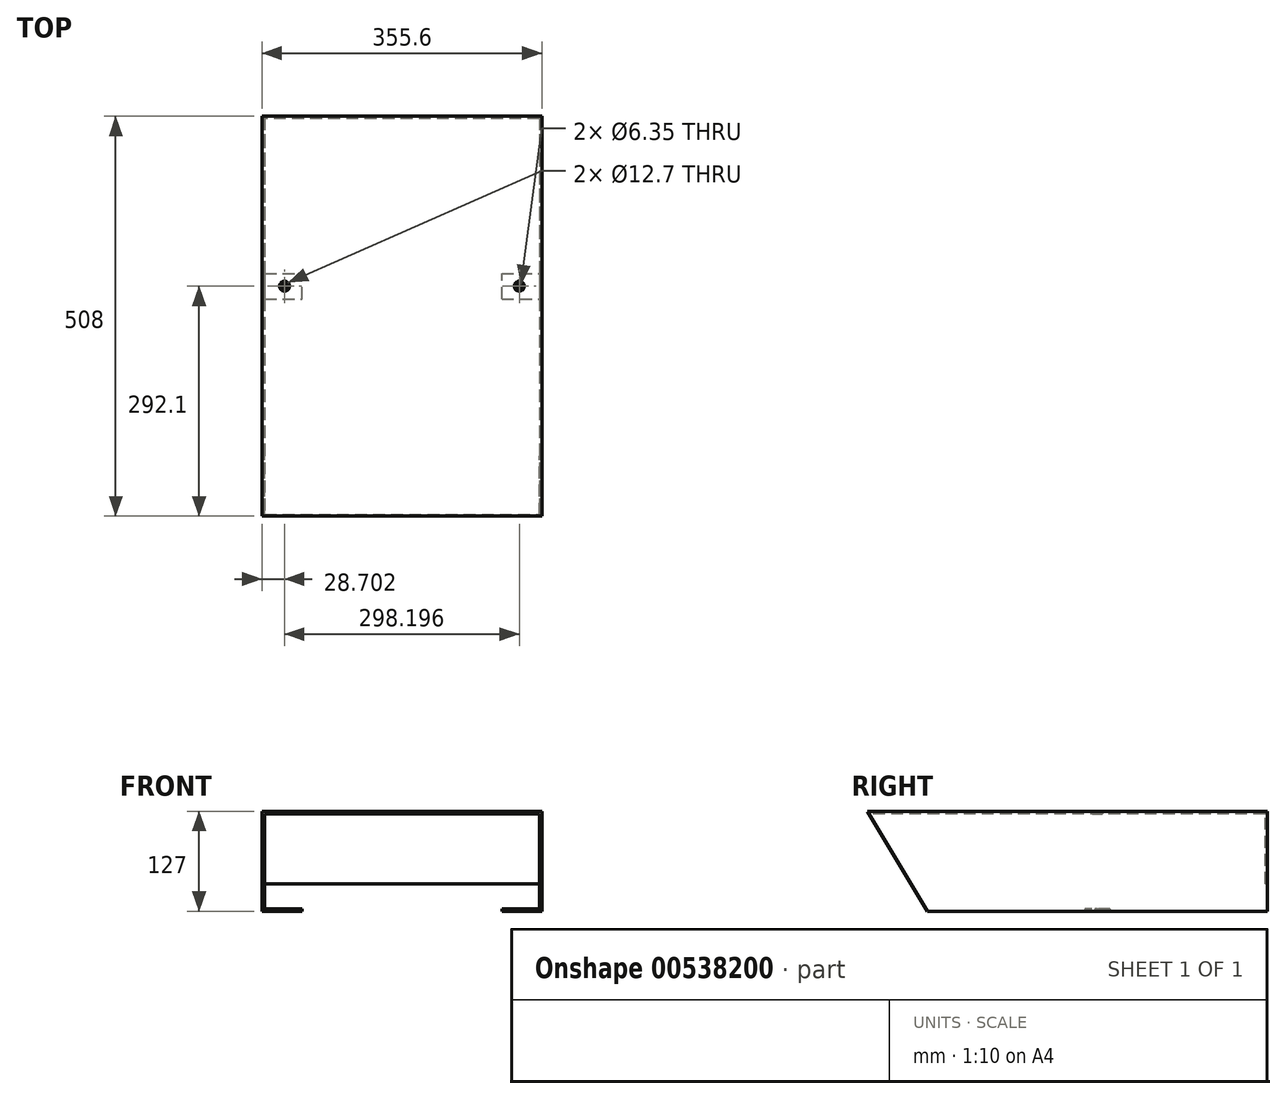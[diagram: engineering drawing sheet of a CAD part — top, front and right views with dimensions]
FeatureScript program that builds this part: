
annotation { "Feature Type Name" : "Feature", "Feature Type Description" : "" }
export const myFeature = defineFeature(function(context is Context, id is Id, definition is map)
    precondition{}
    {
        {
            var Q0;
            Q0=qCreatedBy(makeId("Front.planeOp"),FACE);
            var sketch = newSketch(context, id + "F0", { "sketchPlane" : qUnion([Q0])});
            skLineSegment(sketch, "E0.bottom", {"start": v(-177.8, 63.5) * mm, "end": v(177.8, 63.5) * mm});
            skLineSegment(sketch, "E0.top", {"start": v(-177.8, -63.5) * mm, "end": v(177.8, -63.5) * mm});
            skLineSegment(sketch, "E0.left", {"start": v(-177.8, 63.5) * mm, "end": v(-177.8, -63.5) * mm});
            skLineSegment(sketch, "E0.right", {"start": v(177.8, 63.5) * mm, "end": v(177.8, -63.5) * mm});
            skPoint(sketch, "E0.middle", {"position": v(0, 0) * mm});
            skSolve(sketch);
        }
        {
            var Q0;
            Q0=qCreatedBy(makeId("Front.planeOp"),FACE);
            var sketch = newSketch(context, id + "F1", { "sketchPlane" : qUnion([Q0])});
            skLineSegment(sketch, "E1.0", {"start": v(-177.8, 63.5) * mm, "end": v(-177.8, -63.5) * mm});
            skLineSegment(sketch, "E2.0", {"start": v(-177.8, 63.5) * mm, "end": v(177.8, 63.5) * mm});
            skLineSegment(sketch, "E3.0", {"start": v(177.8, 63.5) * mm, "end": v(177.8, -63.5) * mm});
            skLineSegment(sketch, "E4.0", {"start": v(-174.5, 60.2) * mm, "end": v(-174.5, -63.5) * mm});
            skLineSegment(sketch, "E4.1", {"start": v(-174.5, 60.2) * mm, "end": v(174.5, 60.2) * mm});
            skLineSegment(sketch, "E4.2", {"start": v(174.5, 60.2) * mm, "end": v(174.5, -63.5) * mm});
            skLineSegment(sketch, "E5", {"start": v(-177.8, -63.5) * mm, "end": v(-174.5, -63.5) * mm});
            skLineSegment(sketch, "E6", {"start": v(174.5, -63.5) * mm, "end": v(177.8, -63.5) * mm});
            skSolve(sketch);
        }
        {
            var Q0;
            Q0 = qSketchRegion(id + "F1", true);
            extrude(context, id + "F2", {"entities" : qUnion([Q0]), "endBound" : BoundingType.SYMMETRIC, "oppositeDirection" : true, "depth" : 431.8 * mm, "offsetDistance" : 25.4 * mm});
        }
        {
            var Q0;
            Q0=makeQuery(id+"F2.opExtrude","CAP_FACE",FACE,{"disambiguationData":[OSD([sQuery(id+"F1.wireOp",EDGE,"E1.0"),sQuery(id+"F1.wireOp",EDGE,"E2.0"),sQuery(id+"F1.wireOp",EDGE,"E3.0"),sQuery(id+"F1.wireOp",EDGE,"E4.0"),sQuery(id+"F1.wireOp",EDGE,"E4.1"),sQuery(id+"F1.wireOp",EDGE,"E4.2"),sQuery(id+"F1.wireOp",EDGE,"E5"),sQuery(id+"F1.wireOp",EDGE,"E6")])],"isStart":true});
            extrude(context, id + "F3", {"entities" : qUnion([Q0]), "operationType" : NewBodyOperationType.ADD, "depth" : 76.2 * mm, "offsetDistance" : 25.4 * mm});
        }
        {
            var Q0;
            {var subQ0=sQuery(id+"F1.wireOp",EDGE,"E3.0");Q0=makeQuery(id+"F3.boolean.opBoolean","MERGE",FACE,{"derivedFrom":[makeQuery(id+"F2.opExtrude","SWEPT_FACE",FACE,{"disambiguationData":[OSD([subQ0])]}),makeQuery(id+"F3.opExtrude","SWEPT_FACE",FACE,{"disambiguationData":[OSD([subQ0])]})]});}
            var sketch = newSketch(context, id + "F4", { "sketchPlane" : qUnion([Q0])});
            skLineSegment(sketch, "E7.bottom", {"start": v(215.9, 63.5) * mm, "end": v(-215.9, 63.5) * mm});
            skLineSegment(sketch, "E7.top", {"start": v(215.9, -63.5) * mm, "end": v(-215.9, -63.5) * mm});
            skLineSegment(sketch, "E7.left", {"start": v(215.9, 63.5) * mm, "end": v(215.9, -63.5) * mm});
            skLineSegment(sketch, "E7.right", {"start": v(-215.9, 63.5) * mm, "end": v(-215.9, -63.5) * mm});
            skPoint(sketch, "E7.middle", {"position": v(0, 0) * mm});
            skLineSegment(sketch, "E8", {"start": v(-215.9, -63.5) * mm, "end": v(-292.1, 63.5) * mm});
            skLineSegment(sketch, "E9", {"start": v(-292.1, 63.5) * mm, "end": v(-292.1, -63.5) * mm});
            skLineSegment(sketch, "E10", {"start": v(-292.1, -63.5) * mm, "end": v(-215.9, -63.5) * mm});
            skSolve(sketch);
        }
        {
            var Q0;
            Q0=makeQuery(id+"F4.imprint","IMPRINT",FACE,{"disambiguationData":[TD([[makeQuery(id+"F4.imprint","IMPRINT",EDGE,{"derivedFrom":sQuery(id+"F4.wireOp",EDGE,"E8")}),1.0]])]});
            extrude(context, id + "F5", {"entities" : qUnion([Q0]), "operationType" : NewBodyOperationType.REMOVE, "oppositeDirection" : true, "depth" : 375.92 * mm, "offsetDistance" : 25.4 * mm, "hasSecondDirection" : true, "secondDirectionOppositeDirection" : false, "secondDirectionDepth" : 25.4 * mm});
        }
        {
            var Q0;
            {var subQ0=sQuery(id+"F1.wireOp",EDGE,"E4.0");Q0=makeQuery(id+"F3.boolean.opBoolean","MERGE",FACE,{"derivedFrom":[makeQuery(id+"F2.opExtrude","SWEPT_FACE",FACE,{"disambiguationData":[OSD([subQ0])]}),makeQuery(id+"F3.opExtrude","SWEPT_FACE",FACE,{"disambiguationData":[OSD([subQ0])]})]});}
            var sketch = newSketch(context, id + "F6", { "sketchPlane" : qUnion([Q0])});
            skLineSegment(sketch, "E11", {"start": v(215.9, 60.2) * mm, "end": v(213.1, 60.2) * mm});
            skLineSegment(sketch, "E12", {"start": v(213.1, 60.2) * mm, "end": v(213.1, -28.7) * mm});
            skLineSegment(sketch, "E13", {"start": v(213.1, -28.7) * mm, "end": v(215.9, -28.7) * mm});
            skLineSegment(sketch, "E14", {"start": v(215.9, -28.7) * mm, "end": v(215.9, 60.2) * mm});
            skSolve(sketch);
        }
        {
            var Q0;
            Q0=makeQuery(id+"F6.imprint","IMPRINT",FACE,{"disambiguationData":[TD([[makeQuery(id+"F6.imprint","IMPRINT",EDGE,{"derivedFrom":sQuery(id+"F6.wireOp",EDGE,"E11")}),1.0]])]});
            var Q1;
            {var subQ0=sQuery(id+"F1.wireOp",EDGE,"E4.2");Q1=makeQuery(id+"F3.boolean.opBoolean","MERGE",FACE,{"derivedFrom":[makeQuery(id+"F2.opExtrude","SWEPT_FACE",FACE,{"disambiguationData":[OSD([subQ0])]}),makeQuery(id+"F3.opExtrude","SWEPT_FACE",FACE,{"disambiguationData":[OSD([subQ0])]})]});}
            extrude(context, id + "F7", {"entities" : qUnion([Q0]), "operationType" : NewBodyOperationType.ADD, "endBound" : BoundingType.UP_TO_SURFACE, "depth" : 25.4 * mm, "endBoundEntityFace" : qUnion([Q1]), "offsetDistance" : 25.4 * mm});
        }
        {
            var Q0;
            {var subQ0=sQuery(id+"F1.wireOp",EDGE,"E4.2");Q0=makeQuery(id+"F3.boolean.opBoolean","MERGE",FACE,{"derivedFrom":[makeQuery(id+"F2.opExtrude","SWEPT_FACE",FACE,{"disambiguationData":[OSD([subQ0])]}),makeQuery(id+"F3.opExtrude","SWEPT_FACE",FACE,{"disambiguationData":[OSD([subQ0])]})]});}
            var sketch = newSketch(context, id + "F8", { "sketchPlane" : qUnion([Q0])});
            skPoint(sketch, "E15", {"position": v(0, -63.5) * mm});
            skLineSegment(sketch, "E16.bottom", {"start": v(-16.1, -60.7) * mm, "end": v(16.1, -60.7) * mm});
            skLineSegment(sketch, "E16.left", {"start": v(-16.1, -60.7) * mm, "end": v(-16.1, -63.5) * mm});
            skLineSegment(sketch, "E16.right", {"start": v(16.1, -60.7) * mm, "end": v(16.1, -63.5) * mm});
            skLineSegment(sketch, "E17", {"start": v(16.1, -63.5) * mm, "end": v(-16.1, -63.5) * mm});
            skLineSegment(sketch, "E18", {"start": v(-16.1, -63.5) * mm, "end": v(-16.1, -60.7) * mm});
            skPoint(sketch, "E19.orphan", {"position": v(16.1, -66.3) * mm});
            skPoint(sketch, "E20.orphan", {"position": v(-16.1, -66.3) * mm});
            skSolve(sketch);
        }
        {
            var Q0;
            Q0=makeQuery(id+"F8.imprint","IMPRINT",FACE,{"disambiguationData":[TD([[makeQuery(id+"F8.imprint","IMPRINT",EDGE,{"derivedFrom":sQuery(id+"F8.wireOp",EDGE,"E16.right")}),-1.0]])]});
            var Q1;
            {var subQ0=sQuery(id+"F1.wireOp",EDGE,"E4.0");Q1=makeQuery(id+"F3.boolean.opBoolean","MERGE",FACE,{"derivedFrom":[makeQuery(id+"F2.opExtrude","SWEPT_FACE",FACE,{"disambiguationData":[OSD([subQ0])]}),makeQuery(id+"F3.opExtrude","SWEPT_FACE",FACE,{"disambiguationData":[OSD([subQ0])]})]});}
            extrude(context, id + "F9", {"entities" : qUnion([Q0]), "operationType" : NewBodyOperationType.ADD, "endBound" : BoundingType.UP_TO_SURFACE, "depth" : 25.4 * mm, "endBoundEntityFace" : qUnion([Q1]), "offsetDistance" : 25.4 * mm});
        }
        {
            var Q0;
            {var subQ0=sQuery(id+"F1.wireOp",EDGE,"E6");var subQ1=sQuery(id+"F1.wireOp",EDGE,"E5");Q0=makeQuery(id+"F9.boolean.opBoolean","MERGE",FACE,{"derivedFrom":[makeQuery(id+"F3.boolean.opBoolean","MERGE",FACE,{"derivedFrom":[makeQuery(id+"F2.opExtrude","SWEPT_FACE",FACE,{"disambiguationData":[OSD([subQ1])]}),makeQuery(id+"F3.opExtrude","SWEPT_FACE",FACE,{"disambiguationData":[OSD([subQ1])]})]}),makeQuery(id+"F3.boolean.opBoolean","MERGE",FACE,{"derivedFrom":[makeQuery(id+"F2.opExtrude","SWEPT_FACE",FACE,{"disambiguationData":[OSD([subQ0])]}),makeQuery(id+"F3.opExtrude","SWEPT_FACE",FACE,{"disambiguationData":[OSD([subQ0])]})]}),makeQuery(id+"F9.opExtrude","SWEPT_FACE",FACE,{"disambiguationData":[OSD([sQuery(id+"F8.wireOp",EDGE,"E17")])]})]});}
            var sketch = newSketch(context, id + "F10", { "sketchPlane" : qUnion([Q0])});
            skLineSegment(sketch, "E21.bottom", {"start": v(-127, 16.1) * mm, "end": v(127, 16.1) * mm});
            skLineSegment(sketch, "E21.top", {"start": v(-127, -16.1) * mm, "end": v(127, -16.1) * mm});
            skLineSegment(sketch, "E21.left", {"start": v(-127, 16.1) * mm, "end": v(-127, -16.1) * mm});
            skLineSegment(sketch, "E21.right", {"start": v(127, 16.1) * mm, "end": v(127, -16.1) * mm});
            skPoint(sketch, "E21.middle", {"position": v(0, 0) * mm});
            skSolve(sketch);
        }
        {
            var Q0;
            Q0=makeQuery(id+"F10.imprint","IMPRINT",FACE,{"disambiguationData":[TD([[makeQuery(id+"F10.imprint","IMPRINT",EDGE,{"derivedFrom":sQuery(id+"F10.wireOp",EDGE,"E21.bottom")}),-1.0]])]});
            extrude(context, id + "F11", {"entities" : qUnion([Q0]), "operationType" : NewBodyOperationType.REMOVE, "oppositeDirection" : true, "depth" : 25.4 * mm, "offsetDistance" : 25.4 * mm});
        }
        {
            var Q0;
            {var subQ0=sQuery(id+"F1.wireOp",EDGE,"E3.0");var subQ2=sQuery(id+"F1.wireOp",EDGE,"E6");var subQ3=sQuery(id+"F1.wireOp",EDGE,"E5");Q0=makeQuery(id+"F11.boolean.opBoolean","SPLIT",FACE,{"disambiguationData":[TD([makeQuery(id+"F2.opExtrude","SWEPT_FACE",FACE,{"disambiguationData":[OSD([subQ0])]})])],"derivedFrom":makeQuery(id+"F9.boolean.opBoolean","MERGE",FACE,{"derivedFrom":[makeQuery(id+"F3.boolean.opBoolean","MERGE",FACE,{"derivedFrom":[makeQuery(id+"F2.opExtrude","SWEPT_FACE",FACE,{"disambiguationData":[OSD([subQ3])]}),makeQuery(id+"F3.opExtrude","SWEPT_FACE",FACE,{"disambiguationData":[OSD([subQ3])]})]}),makeQuery(id+"F3.boolean.opBoolean","MERGE",FACE,{"derivedFrom":[makeQuery(id+"F2.opExtrude","SWEPT_FACE",FACE,{"disambiguationData":[OSD([subQ2])]}),makeQuery(id+"F3.opExtrude","SWEPT_FACE",FACE,{"disambiguationData":[OSD([subQ2])]})]}),makeQuery(id+"F9.opExtrude","SWEPT_FACE",FACE,{"disambiguationData":[OSD([sQuery(id+"F8.wireOp",EDGE,"E17")])]})]})});}
            var sketch = newSketch(context, id + "F12", { "sketchPlane" : qUnion([Q0])});
            skPoint(sketch, "E22", {"position": v(174.5, 0) * mm});
            skLineSegment(sketch, "E23", {"start": v(174.5, 0) * mm, "end": v(149.1, 0) * mm});
            skCircle(sketch, "E24", {"center": v(149.1, 0) * mm, "radius": 3.18 * mm});
            skSolve(sketch);
        }
        {
            var Q0;
            Q0=makeQuery(id+"F12.imprint","IMPRINT",FACE,{"disambiguationData":[TD([[makeQuery(id+"F12.imprint","IMPRINT",EDGE,{"derivedFrom":sQuery(id+"F12.wireOp",EDGE,"E24")}),1.0]])]});
            extrude(context, id + "F13", {"entities" : qUnion([Q0]), "operationType" : NewBodyOperationType.REMOVE, "oppositeDirection" : true, "depth" : 25.4 * mm, "offsetDistance" : 25.4 * mm});
        }
        {
            var Q0;
            {var subQ0=sQuery(id+"F1.wireOp",EDGE,"E1.0");var subQ1=sQuery(id+"F1.wireOp",EDGE,"E6");var subQ2=sQuery(id+"F1.wireOp",EDGE,"E5");Q0=makeQuery(id+"F11.boolean.opBoolean","SPLIT",FACE,{"disambiguationData":[TD([makeQuery(id+"F2.opExtrude","SWEPT_FACE",FACE,{"disambiguationData":[OSD([subQ0])]})])],"derivedFrom":makeQuery(id+"F9.boolean.opBoolean","MERGE",FACE,{"derivedFrom":[makeQuery(id+"F3.boolean.opBoolean","MERGE",FACE,{"derivedFrom":[makeQuery(id+"F2.opExtrude","SWEPT_FACE",FACE,{"disambiguationData":[OSD([subQ2])]}),makeQuery(id+"F3.opExtrude","SWEPT_FACE",FACE,{"disambiguationData":[OSD([subQ2])]})]}),makeQuery(id+"F3.boolean.opBoolean","MERGE",FACE,{"derivedFrom":[makeQuery(id+"F2.opExtrude","SWEPT_FACE",FACE,{"disambiguationData":[OSD([subQ1])]}),makeQuery(id+"F3.opExtrude","SWEPT_FACE",FACE,{"disambiguationData":[OSD([subQ1])]})]}),makeQuery(id+"F9.opExtrude","SWEPT_FACE",FACE,{"disambiguationData":[OSD([sQuery(id+"F8.wireOp",EDGE,"E17")])]})]})});}
            var sketch = newSketch(context, id + "F14", { "sketchPlane" : qUnion([Q0])});
            skPoint(sketch, "E25", {"position": v(-174.5, 0) * mm});
            skLineSegment(sketch, "E26", {"start": v(-174.5, 0) * mm, "end": v(-149.1, 0) * mm});
            skCircle(sketch, "E27", {"center": v(-149.1, 0) * mm, "radius": 3.18 * mm});
            skSolve(sketch);
        }
        {
            var Q0;
            Q0=makeQuery(id+"F14.imprint","IMPRINT",FACE,{"disambiguationData":[TD([[makeQuery(id+"F14.imprint","IMPRINT",EDGE,{"derivedFrom":sQuery(id+"F14.wireOp",EDGE,"E27")}),1.0]])]});
            extrude(context, id + "F15", {"entities" : qUnion([Q0]), "operationType" : NewBodyOperationType.REMOVE, "oppositeDirection" : true, "depth" : 25.4 * mm, "offsetDistance" : 25.4 * mm});
        }
        {
            var Q0;
            {var subQ0=sQuery(id+"F1.wireOp",EDGE,"E4.1");Q0=makeQuery(id+"F3.boolean.opBoolean","MERGE",FACE,{"derivedFrom":[makeQuery(id+"F2.opExtrude","SWEPT_FACE",FACE,{"disambiguationData":[OSD([subQ0])]}),makeQuery(id+"F3.opExtrude","SWEPT_FACE",FACE,{"disambiguationData":[OSD([subQ0])]})]});}
            var sketch = newSketch(context, id + "F16", { "sketchPlane" : qUnion([Q0])});
            skCircle(sketch, "E28", {"center": v(149.1, 0) * mm, "radius": 6.35 * mm});
            skCircle(sketch, "E29", {"center": v(-149.1, 0) * mm, "radius": 6.35 * mm});
            skSolve(sketch);
        }
        {
            var Q0;
            Q0 = qSketchRegion(id + "F16", true);
            extrude(context, id + "F17", {"entities" : qUnion([Q0]), "operationType" : NewBodyOperationType.REMOVE, "oppositeDirection" : true, "depth" : 25.4 * mm, "offsetDistance" : 25.4 * mm});
        }
    });
